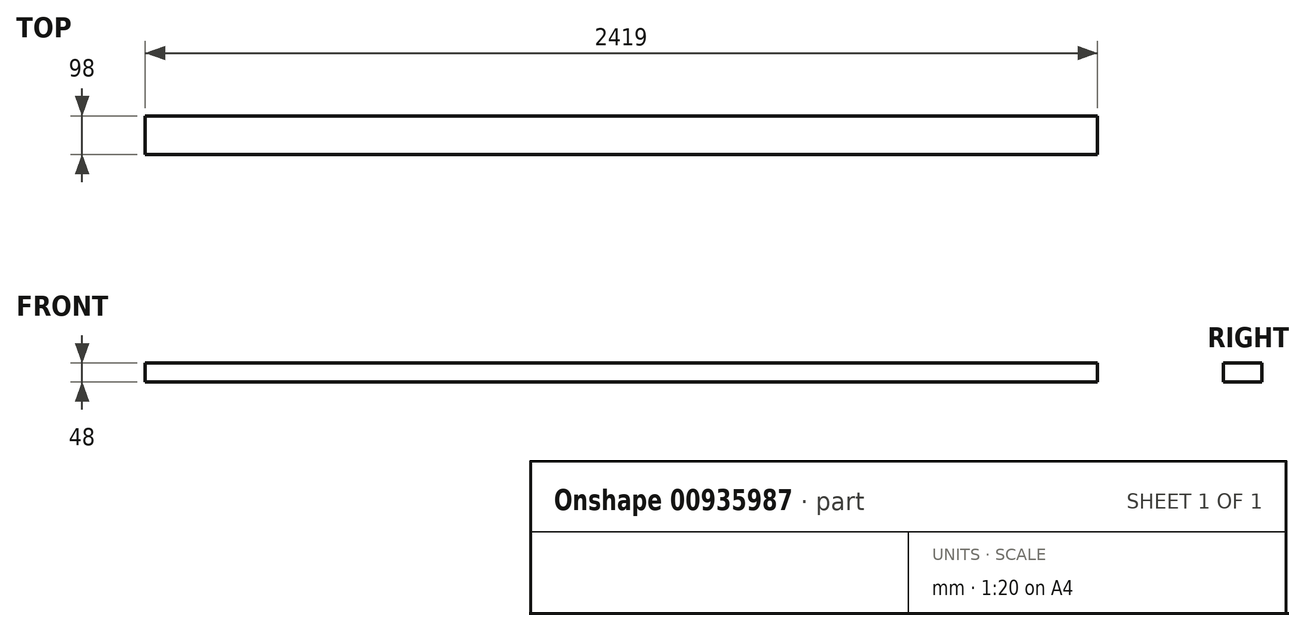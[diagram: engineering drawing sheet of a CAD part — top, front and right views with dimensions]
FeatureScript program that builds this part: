
annotation { "Feature Type Name" : "Feature", "Feature Type Description" : "" }
export const myFeature = defineFeature(function(context is Context, id is Id, definition is map)
    precondition{}
    {
        {
            var Q0;
            Q0=qCreatedBy(makeId("Right.planeOp"),FACE);
            var sketch = newSketch(context, id + "F0", { "sketchPlane" : qUnion([Q0])});
            skLineSegment(sketch, "E0.bottom", {"start": v(49, -24) * mm, "end": v(-49, -24) * mm});
            skLineSegment(sketch, "E0.top", {"start": v(49, 24) * mm, "end": v(-49, 24) * mm});
            skLineSegment(sketch, "E0.left", {"start": v(49, -24) * mm, "end": v(49, 24) * mm});
            skLineSegment(sketch, "E0.right", {"start": v(-49, -24) * mm, "end": v(-49, 24) * mm});
            skPoint(sketch, "E0.middle", {"position": v(0, 0) * mm});
            skSolve(sketch);
        }
        {
            assignVariable(context, id + "F1", {"name" : "Length", "anyValue" : 2419});
        }
        {
            var Q0;
            Q0=qSketchRegion(id+"F0",true);
            extrude(context, id + "F2", {"entities" : qUnion([Q0]), "depth" : (getVariable(context, 'Length')) * mm, "offsetDistance" : 25 * mm});
        }
    });
